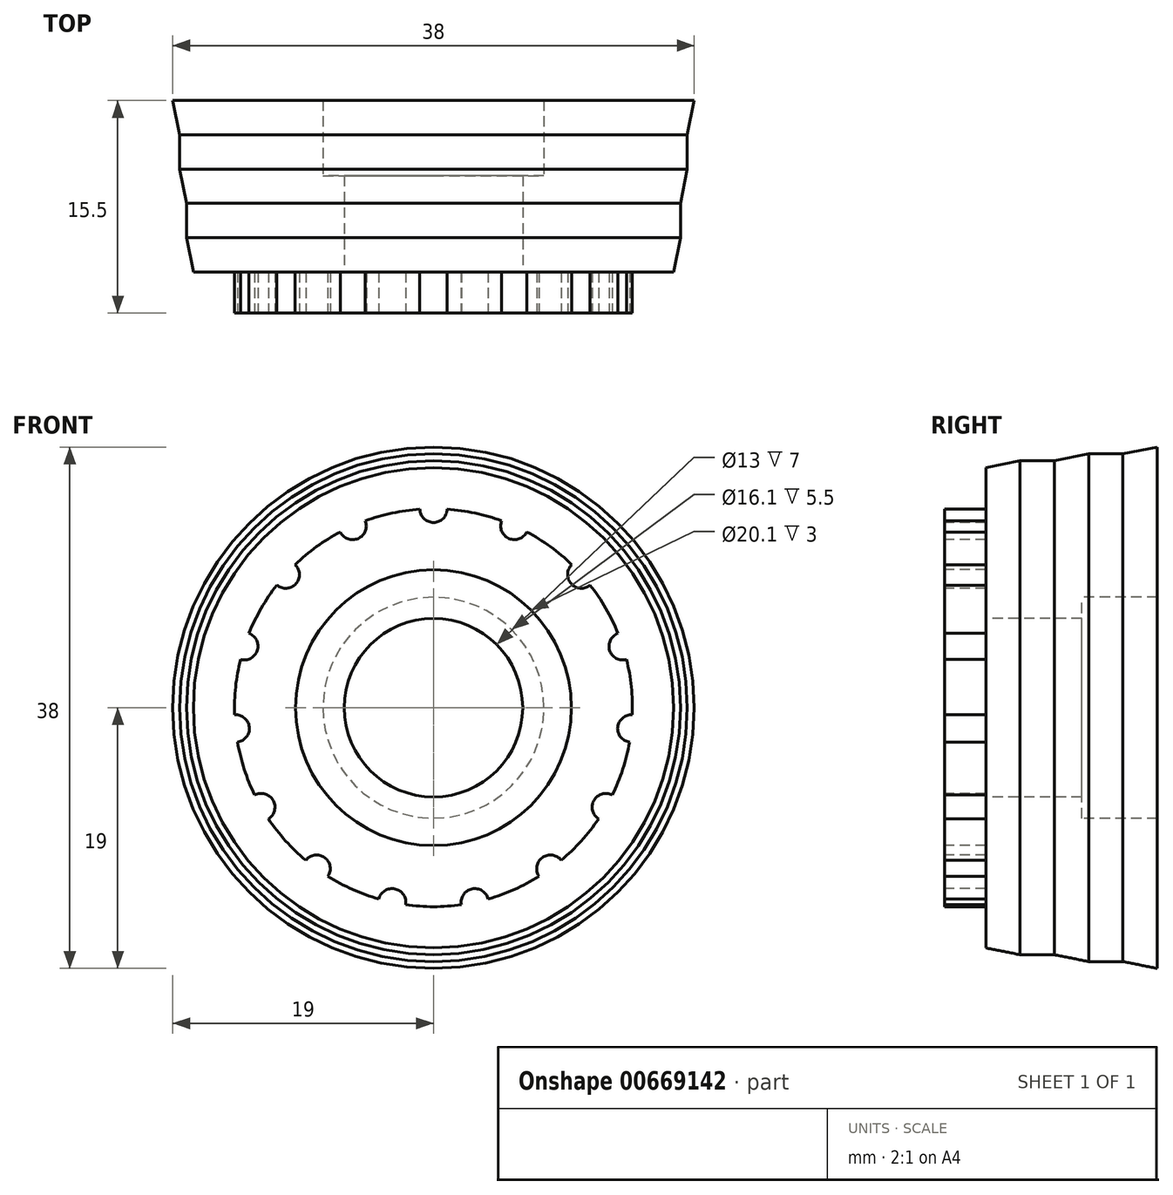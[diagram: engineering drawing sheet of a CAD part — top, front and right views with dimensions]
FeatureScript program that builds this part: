
annotation { "Feature Type Name" : "Feature", "Feature Type Description" : "" }
export const myFeature = defineFeature(function(context is Context, id is Id, definition is map)
    precondition{}
    {
        {
            var Q0;
            Q0=qCreatedBy(makeId("Right.planeOp"),FACE);
            var sketch = newSketch(context, id + "F0", { "sketchPlane" : qUnion([Q0])});
            skLineSegment(sketch, "E0", {"start": v(0, 0) * mm, "end": v(41.77, 0) * mm, "construction": true});
            skLineSegment(sketch, "E1", {"start": v(7, 6.5) * mm, "end": v(0, 6.5) * mm});
            skLineSegment(sketch, "E2", {"start": v(0, 6.5) * mm, "end": v(0, 10.05) * mm});
            skLineSegment(sketch, "E3", {"start": v(0, 10.05) * mm, "end": v(-3, 10.05) * mm});
            skLineSegment(sketch, "E4", {"start": v(-3, 10.05) * mm, "end": v(-3, 14.5) * mm});
            skLineSegment(sketch, "E5", {"start": v(-3, 14.5) * mm, "end": v(0, 14.5) * mm});
            skLineSegment(sketch, "E6", {"start": v(0, 14.5) * mm, "end": v(0, 17.5) * mm});
            skLineSegment(sketch, "E7", {"start": v(0, 17.5) * mm, "end": v(2.5, 18) * mm});
            skLineSegment(sketch, "E8", {"start": v(2.5, 18) * mm, "end": v(5, 18) * mm});
            skLineSegment(sketch, "E9", {"start": v(5, 18) * mm, "end": v(7.5, 18.5) * mm});
            skLineSegment(sketch, "E10", {"start": v(7.5, 18.5) * mm, "end": v(10, 18.5) * mm});
            skLineSegment(sketch, "E11", {"start": v(10, 18.5) * mm, "end": v(12.5, 19) * mm});
            skLineSegment(sketch, "E12", {"start": v(12.5, 19) * mm, "end": v(12.5, 8.05) * mm});
            skLineSegment(sketch, "E13", {"start": v(7, 8.05) * mm, "end": v(12.5, 8.05) * mm});
            skLineSegment(sketch, "E14", {"start": v(7, 8.05) * mm, "end": v(7, 6.5) * mm});
            skSolve(sketch);
        }
        {
            var Q0;
            Q0 = qSketchRegion(id + "F0", true);
            var Q1;
            Q1=sQuery(id+"F0.wireOp",EDGE,"E0");
            revolve(context, id + "F1", {"entities" : qUnion([Q0]), "axis" : qUnion([Q1]), "revolveType" : RevolveType.FULL});
        }
        {
            var Q0;
            Q0=makeQuery(id+"F1.opRevolve","SWEPT_FACE",FACE,{"disambiguationData":[OSD([sQuery(id+"F0.wireOp",EDGE,"E4")])]});
            var sketch = newSketch(context, id + "F2", { "sketchPlane" : qUnion([Q0])});
            skArc(sketch, "E15", {"start": v(-1, 14.47) * mm, "mid": v(0, 13.5) * mm, "end": v(1, 14.47) * mm});
            skArc(sketch, "E16", {"start": v(1, 14.47) * mm, "mid": v(0, 14.5) * mm, "end": v(-1, 14.47) * mm});
            skArc(sketch, "E17.1.0", {"start": v(-6.8, 12.8) * mm, "mid": v(-5.5, 12.33) * mm, "end": v(-4.97, 13.62) * mm});
            skArc(sketch, "E17.1.1", {"start": v(-4.97, 13.62) * mm, "mid": v(-5.9, 13.25) * mm, "end": v(-6.8, 12.8) * mm});
            skArc(sketch, "E17.2.0", {"start": v(-11.42, 8.94) * mm, "mid": v(-10.03, 9.03) * mm, "end": v(-10.08, 10.42) * mm});
            skArc(sketch, "E17.2.1", {"start": v(-10.08, 10.42) * mm, "mid": v(-10.78, 9.7) * mm, "end": v(-11.42, 8.94) * mm});
            skArc(sketch, "E17.3.0", {"start": v(-14.07, 3.52) * mm, "mid": v(-12.84, 4.17) * mm, "end": v(-13.45, 5.42) * mm});
            skArc(sketch, "E17.3.1", {"start": v(-13.45, 5.42) * mm, "mid": v(-13.8, 4.48) * mm, "end": v(-14.07, 3.52) * mm});
            skArc(sketch, "E17.4.0", {"start": v(-14.28, -2.5) * mm, "mid": v(-13.43, -1.41) * mm, "end": v(-14.5, -0.52) * mm});
            skArc(sketch, "E17.4.1", {"start": v(-14.5, -0.52) * mm, "mid": v(-14.42, -1.52) * mm, "end": v(-14.28, -2.5) * mm});
            skArc(sketch, "E17.5.0", {"start": v(-12.03, -8.1) * mm, "mid": v(-11.7, -6.75) * mm, "end": v(-13.03, -6.37) * mm});
            skArc(sketch, "E17.5.1", {"start": v(-13.03, -6.37) * mm, "mid": v(-12.56, -7.25) * mm, "end": v(-12.03, -8.1) * mm});
            skArc(sketch, "E17.6.0", {"start": v(-7.7, -12.3) * mm, "mid": v(-7.93, -10.92) * mm, "end": v(-9.31, -11.12) * mm});
            skArc(sketch, "E17.6.1", {"start": v(-9.31, -11.12) * mm, "mid": v(-8.52, -11.73) * mm, "end": v(-7.7, -12.3) * mm});
            skArc(sketch, "E17.7.0", {"start": v(-2.03, -14.36) * mm, "mid": v(-2.8, -13.2) * mm, "end": v(-3.99, -13.94) * mm});
            skArc(sketch, "E17.7.1", {"start": v(-3.99, -13.94) * mm, "mid": v(-3.01, -14.18) * mm, "end": v(-2.03, -14.36) * mm});
            skArc(sketch, "E17.8.0", {"start": v(3.99, -13.94) * mm, "mid": v(2.8, -13.2) * mm, "end": v(2.03, -14.36) * mm});
            skArc(sketch, "E17.8.1", {"start": v(2.03, -14.36) * mm, "mid": v(3.01, -14.18) * mm, "end": v(3.99, -13.94) * mm});
            skArc(sketch, "E17.9.0", {"start": v(9.31, -11.12) * mm, "mid": v(7.93, -10.92) * mm, "end": v(7.7, -12.3) * mm});
            skArc(sketch, "E17.9.1", {"start": v(7.7, -12.3) * mm, "mid": v(8.52, -11.73) * mm, "end": v(9.31, -11.12) * mm});
            skArc(sketch, "E17.10.0", {"start": v(13.03, -6.37) * mm, "mid": v(11.7, -6.75) * mm, "end": v(12.03, -8.1) * mm});
            skArc(sketch, "E17.10.1", {"start": v(12.03, -8.1) * mm, "mid": v(12.56, -7.25) * mm, "end": v(13.03, -6.37) * mm});
            skArc(sketch, "E17.11.0", {"start": v(14.5, -0.52) * mm, "mid": v(13.43, -1.41) * mm, "end": v(14.28, -2.5) * mm});
            skArc(sketch, "E17.11.1", {"start": v(14.28, -2.5) * mm, "mid": v(14.42, -1.52) * mm, "end": v(14.5, -0.52) * mm});
            skArc(sketch, "E17.12.0", {"start": v(13.45, 5.42) * mm, "mid": v(12.84, 4.17) * mm, "end": v(14.07, 3.52) * mm});
            skArc(sketch, "E17.12.1", {"start": v(14.07, 3.52) * mm, "mid": v(13.8, 4.48) * mm, "end": v(13.45, 5.42) * mm});
            skArc(sketch, "E17.13.0", {"start": v(10.08, 10.42) * mm, "mid": v(10.03, 9.03) * mm, "end": v(11.42, 8.94) * mm});
            skArc(sketch, "E17.13.1", {"start": v(11.42, 8.94) * mm, "mid": v(10.78, 9.7) * mm, "end": v(10.08, 10.42) * mm});
            skArc(sketch, "E17.14.0", {"start": v(4.97, 13.62) * mm, "mid": v(5.5, 12.33) * mm, "end": v(6.8, 12.8) * mm});
            skArc(sketch, "E17.14.1", {"start": v(6.8, 12.8) * mm, "mid": v(5.9, 13.25) * mm, "end": v(4.97, 13.62) * mm});
            skSolve(sketch);
        }
        {
            var Q0;
            Q0 = qSketchRegion(id + "F2", true);
            extrude(context, id + "F3", {"entities" : qUnion([Q0]), "operationType" : NewBodyOperationType.REMOVE, "oppositeDirection" : true, "depth" : 3 * mm, "offsetDistance" : 25 * mm});
        }
    });
